# Revit family: Drain_Trench_Polymer_6-Inch_Wide_Reveal-Zurn-ZF806
name_source: partatom
category: Plumbing Fixtures
units: mm (PartAtom-declared; Revit-internal decimal feet)

## family parameters
Always vertical = Yes
Cut with Voids When Loaded = No
Maintain Annotation Orientation = No
OmniClass Number = 23.70.50.21.24.14
OmniClass Title = Deck Waste Water Drains
Part Type = Normal
Room Calculation Point = No
Round Connector Dimension = Use Diameter
Shared = No
Work Plane-Based = No

## types (36) — shared parameters
Assembly Code = D2030300
CW Connection = No
Channel length = 120 "
Default Elevation = 1 "
Description = 6 [159] WIDE REVEAL FIBER REINFORCED POLYMER TRENCH DRAIN SYSTEM
HW Connection = No
Inside Width = 4 "
Main Material = Polymer - Zurn - Fiber Reinforced Blue
Manufacturer = Zurn Water, LLC
Manufacurer Brand = Zurn
Modified Date = 04/04/25
Overlap length = 122.5 "
Product Documentation Link = https://files.zurn.com
Product Installation Sheet = https://www.zurn.com
Product Page URL = https://www.zurn.com
Product data url = https://www.bimobject.com
URL = www.zurn.com
Vent Connection = No
Waste Connection = Yes
Width = 5.781 "
zero-valued in all types: CWFU, HWFU, WFU

## per-type parameters (varying)
| type | Deep Invert Height | Flow | Frame Material | Grate Material | Hardware Material | Model | Shallow Invert Height |
| ZF806-120 x 4.75 x 5.65 (1002) | 5.65 " | 146 GPM | Ductile Iron-Zurn-Polished | Ductile Iron-Zurn-Polished | Ductile Iron-Zurn-Polished | ZF806 | 4.75 " |
| ZF806-120 x 5.65 x 5.65 (1002N) | 5.65 " | 146 GPM | Ductile Iron-Zurn-Polished | Ductile Iron-Zurn-Polished | Ductile Iron-Zurn-Polished | ZF806 | 5.65 " |
| ZF806-120 x 5.65 x 6.55 (1003) | 6.55 " | 192 GPM | Ductile Iron-Zurn-Polished | Ductile Iron-Zurn-Polished | Ductile Iron-Zurn-Polished | ZF806 | 5.65 " |
| ZF806-120 x 6.55 x 7.45 (1004) | 7.45 " | 238 GPM | Ductile Iron-Zurn-Polished | Ductile Iron-Zurn-Polished | Ductile Iron-Zurn-Polished | ZF806 | 6.55 " |
| ZF806-120 x 7.45 x 7.45(1004N) | 7.45 " | 238 GPM | Ductile Iron-Zurn-Polished | Ductile Iron-Zurn-Polished | Ductile Iron-Zurn-Polished | ZF806 | 7.45 " |
| ZF806-120 x 7.45 x 8.35 (1005) | 8.35 " | 285 GPM | Ductile Iron-Zurn-Polished | Ductile Iron-Zurn-Polished | Ductile Iron-Zurn-Polished | ZF806 | 7.45 " |
| ZF806-120 x 8.35 x 9.25 (1006) | 9.25 " | 332 GPM | Ductile Iron-Zurn-Polished | Ductile Iron-Zurn-Polished | Ductile Iron-Zurn-Polished | ZF806 | 8.35 " |
| ZF806-120 x 9.25 x 10.15 (1007) | 10.15 " | 379 GPM | Ductile Iron-Zurn-Polished | Ductile Iron-Zurn-Polished | Ductile Iron-Zurn-Polished | ZF806 | 9.25 " |
| ZF806-120 x 10.15 x 11.05 (1008) | 11.05 " | 427 GPM | Ductile Iron-Zurn-Polished | Ductile Iron-Zurn-Polished | Ductile Iron-Zurn-Polished | ZF806 | 10.15 " |
| ZF806-120 x 11.05 x 11.05 (1008N) | 11.05 " | 427 GPM | Ductile Iron-Zurn-Polished | Ductile Iron-Zurn-Polished | Ductile Iron-Zurn-Polished | ZF806 | 11.05 " |
| ZF806-120 x 11.05 x 11.95 (1009) | 11.95 " | 475 GPM | Ductile Iron-Zurn-Polished | Ductile Iron-Zurn-Polished | Ductile Iron-Zurn-Polished | ZF806 | 11.05 " |
| ZF806-120 x 11.95 x 12.85 (1010) | 12.85 " | 523 GPM | Ductile Iron-Zurn-Polished | Ductile Iron-Zurn-Polished | Ductile Iron-Zurn-Polished | ZF806 | 11.95 " |
| ZF806-HDG-120 x 4.75 x 5.65 (1002) | 5.65 " | 146 GPM | Galvanized Ductile -Zurn-Polished | Galvanized Ductile -Zurn-Polished | Galvanized Ductile -Zurn-Polished | ZF806-HDG | 4.75 " |
| ZF806-HDG-120 x 5.65 x 5.65 (1002N) | 5.65 " | 146 GPM | Galvanized Ductile -Zurn-Polished | Galvanized Ductile -Zurn-Polished | Galvanized Ductile -Zurn-Polished | ZF806-HDG | 5.65 " |
| ZF806-HDG-120 x 5.65 x 6.55 (1003) | 6.55 " | 192 GPM | Galvanized Ductile -Zurn-Polished | Galvanized Ductile -Zurn-Polished | Galvanized Ductile -Zurn-Polished | ZF806-HDG | 5.65 " |
| ZF806-HDG-120 x 6.55 x 7.45 (1004) | 7.45 " | 238 GPM | Galvanized Ductile -Zurn-Polished | Galvanized Ductile -Zurn-Polished | Galvanized Ductile -Zurn-Polished | ZF806-HDG | 6.55 " |
| ZF806-HDG-120 x 7.45 x 7.45(1004N) | 7.45 " | 238 GPM | Galvanized Ductile -Zurn-Polished | Galvanized Ductile -Zurn-Polished | Galvanized Ductile -Zurn-Polished | ZF806-HDG | 7.45 " |
| ZF806-HDG-120 x 7.45 x 8.35 (1005) | 8.35 " | 285 GPM | Galvanized Ductile -Zurn-Polished | Galvanized Ductile -Zurn-Polished | Galvanized Ductile -Zurn-Polished | ZF806-HDG | 7.45 " |
| ZF806-HDG-120 x 8.35 x 9.25 (1006) | 9.25 " | 332 GPM | Galvanized Ductile -Zurn-Polished | Galvanized Ductile -Zurn-Polished | Galvanized Ductile -Zurn-Polished | ZF806-HDG | 8.35 " |
| ZF806-HDG-120 x 9.25 x 10.15 (1007) | 10.15 " | 379 GPM | Galvanized Ductile -Zurn-Polished | Galvanized Ductile -Zurn-Polished | Galvanized Ductile -Zurn-Polished | ZF806-HDG | 9.25 " |
| ZF806-HDG-120 x 10.15 x 11.05 (1008) | 11.05 " | 427 GPM | Galvanized Ductile -Zurn-Polished | Galvanized Ductile -Zurn-Polished | Galvanized Ductile -Zurn-Polished | ZF806-HDG | 10.15 " |
| ZF806-HDG-120 x 11.05 x 11.05 (1008N) | 11.05 " | 427 GPM | Galvanized Ductile -Zurn-Polished | Galvanized Ductile -Zurn-Polished | Galvanized Ductile -Zurn-Polished | ZF806-HDG | 11.05 " |
| ZF806-HDG-120 x 11.05 x 11.95 (1009) | 11.95 " | 475 GPM | Galvanized Ductile -Zurn-Polished | Galvanized Ductile -Zurn-Polished | Galvanized Ductile -Zurn-Polished | ZF806-HDG | 11.05 " |
| ZF806-HDG-120 x 11.95 x 12.85 (1010) | 12.85 " | 523 GPM | Galvanized Ductile -Zurn-Polished | Galvanized Ductile -Zurn-Polished | Galvanized Ductile -Zurn-Polished | ZF806-HDG | 11.95 " |
| ZF806-HDS-120 x 4.75 x 5.65 (1002) | 5.65 " | 146 GPM | Stainless Steel_Zurn_Polished | Stainless Steel_Zurn_Polished | Stainless Steel_Zurn_Polished | ZF806-HDS | 4.75 " |
| ZF806-HDS-120 x 5.65 x 5.65 (1002N) | 5.65 " | 146 GPM | Stainless Steel_Zurn_Polished | Stainless Steel_Zurn_Polished | Stainless Steel_Zurn_Polished | ZF806-HDS | 5.65 " |
| ZF806-HDS-120 x 5.65 x 6.55 (1003) | 6.55 " | 192 GPM | Stainless Steel_Zurn_Polished | Stainless Steel_Zurn_Polished | Stainless Steel_Zurn_Polished | ZF806-HDS | 5.65 " |
| ZF806-HDS-120 x 6.55 x 7.45 (1004) | 7.45 " | 238 GPM | Stainless Steel_Zurn_Polished | Stainless Steel_Zurn_Polished | Stainless Steel_Zurn_Polished | ZF806-HDS | 6.55 " |
| ZF806-HDS-120 x 7.45 x 7.45(1004N) | 7.45 " | 238 GPM | Stainless Steel_Zurn_Polished | Stainless Steel_Zurn_Polished | Stainless Steel_Zurn_Polished | ZF806-HDS | 7.45 " |
| ZF806-HDS-120 x 7.45 x 8.35 (1005) | 8.35 " | 285 GPM | Stainless Steel_Zurn_Polished | Stainless Steel_Zurn_Polished | Stainless Steel_Zurn_Polished | ZF806-HDS | 7.45 " |
| ZF806-HDS-120 x 8.35 x 9.25 (1006) | 9.25 " | 332 GPM | Stainless Steel_Zurn_Polished | Stainless Steel_Zurn_Polished | Stainless Steel_Zurn_Polished | ZF806-HDS | 8.35 " |
| ZF806-HDS-120 x 9.25 x 10.15 (1007) | 10.15 " | 379 GPM | Stainless Steel_Zurn_Polished | Stainless Steel_Zurn_Polished | Stainless Steel_Zurn_Polished | ZF806-HDS | 9.25 " |
| ZF806-HDS-120 x 10.15 x 11.05 (1008) | 11.05 " | 427 GPM | Stainless Steel_Zurn_Polished | Stainless Steel_Zurn_Polished | Stainless Steel_Zurn_Polished | ZF806-HDS | 10.15 " |
| ZF806-HDS-120 x 11.05 x 11.05 (1008N) | 11.05 " | 427 GPM | Stainless Steel_Zurn_Polished | Stainless Steel_Zurn_Polished | Stainless Steel_Zurn_Polished | ZF806-HDS | 11.05 " |
| ZF806-HDS-120 x 11.05 x 11.95 (1009) | 11.95 " | 475 GPM | Stainless Steel_Zurn_Polished | Stainless Steel_Zurn_Polished | Stainless Steel_Zurn_Polished | ZF806-HDS | 11.05 " |
| ZF806-HDS-120 x 11.95 x 12.85 (1010) | 12.85 " | 523 GPM | Stainless Steel_Zurn_Polished | Stainless Steel_Zurn_Polished | Stainless Steel_Zurn_Polished | ZF806-HDS | 11.95 " |

note: column(s) folded — value = type name in every type: Type Comments

## geometry (parser evidence)
native form markers: Sweep x4
no freeform markers — native parametric forms only
